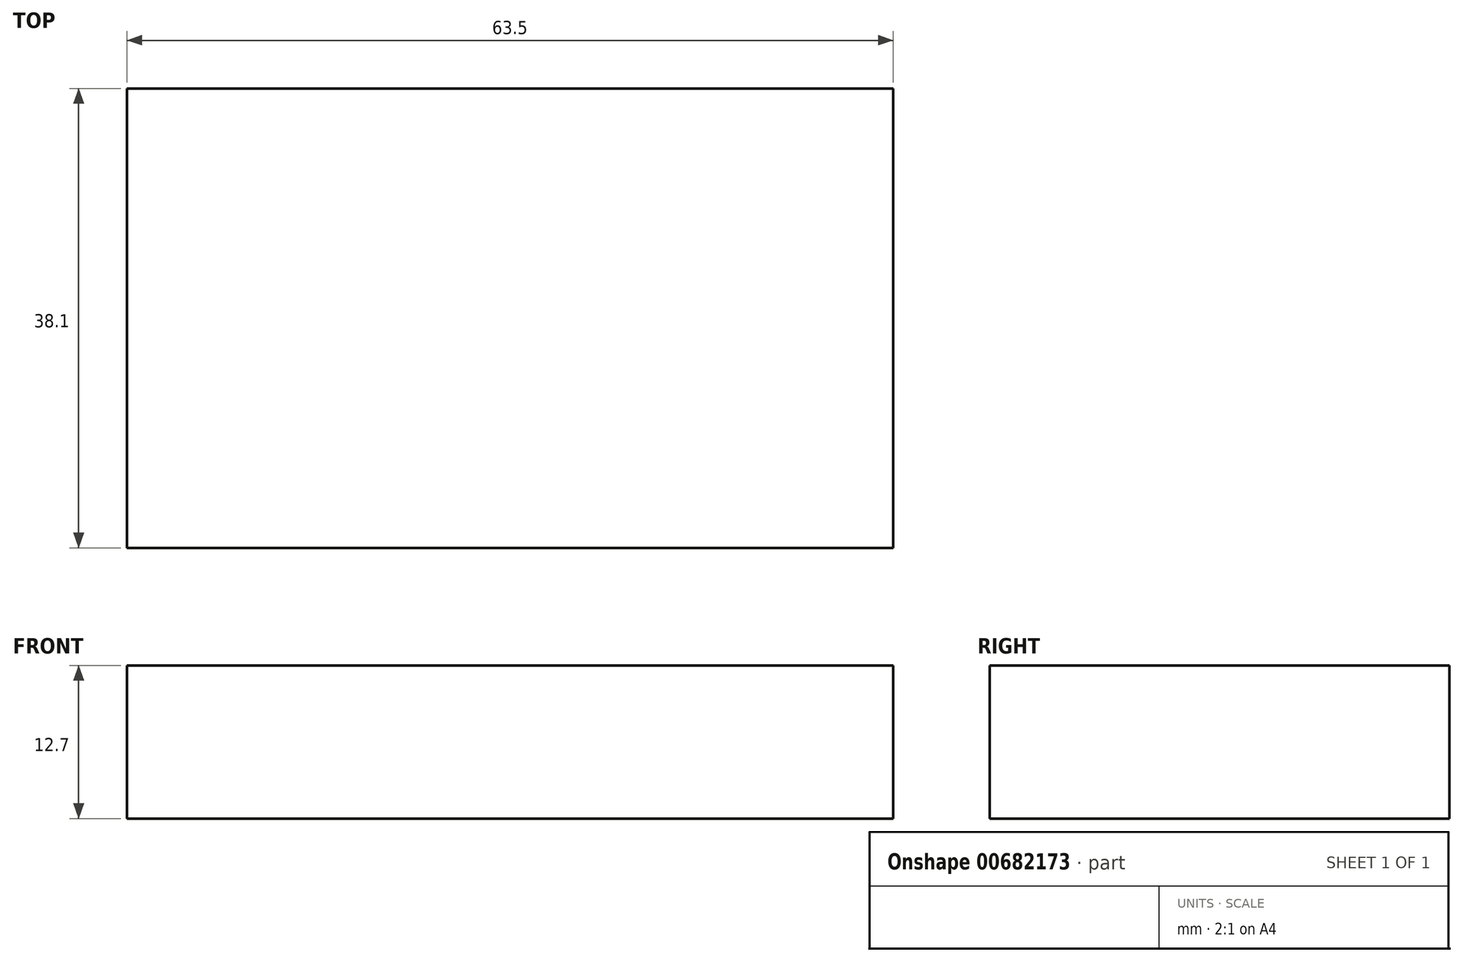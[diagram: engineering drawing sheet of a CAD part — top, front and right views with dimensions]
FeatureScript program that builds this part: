
annotation { "Feature Type Name" : "Feature", "Feature Type Description" : "" }
export const myFeature = defineFeature(function(context is Context, id is Id, definition is map)
    precondition{}
    {
        {
            var Q0;
            Q0=qCreatedBy(makeId("Top.planeOp"),FACE);
            var sketch = newSketch(context, id + "F0", { "sketchPlane" : qUnion([Q0])});
            skLineSegment(sketch, "E0.bottom", {"start": v(31.75, 19.05) * mm, "end": v(-31.75, 19.05) * mm});
            skLineSegment(sketch, "E0.top", {"start": v(31.75, -19.05) * mm, "end": v(-31.75, -19.05) * mm});
            skLineSegment(sketch, "E0.left", {"start": v(31.75, 19.05) * mm, "end": v(31.75, -19.05) * mm});
            skLineSegment(sketch, "E0.right", {"start": v(-31.75, 19.05) * mm, "end": v(-31.75, -19.05) * mm});
            skPoint(sketch, "E0.middle", {"position": v(0, 0) * mm});
            skSolve(sketch);
        }
        {
            var Q0;
            Q0 = qSketchRegion(id + "F0", true);
            extrude(context, id + "F1", {"entities" : qUnion([Q0]), "depth" : 12.7 * mm, "offsetDistance" : 25.4 * mm});
        }
    });
